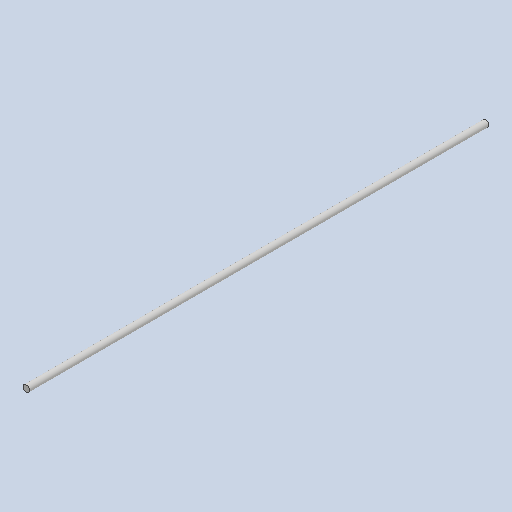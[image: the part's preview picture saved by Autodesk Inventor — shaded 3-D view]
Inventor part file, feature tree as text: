
AUTODESK INVENTOR PART (.ipt)
format: ipt  version: 2023 (Build 270158000, 158)  size: 81,920 bytes
history: native  units: mm
features: extrude x1, sketch x1
ambient origin geometry x8: Origin, YZ Plane, XZ Plane, XY Plane, X Axis, Y Axis, Z Axis, Center Point
bodies: Solid1 (feature_tree)
feature tree (2):
  extrude  "Extrusion1"  Depth=560.0mm
  sketch  "Sketch1"  dims[d0=8.0mm d1=560.0mm d2=0.0mm]
